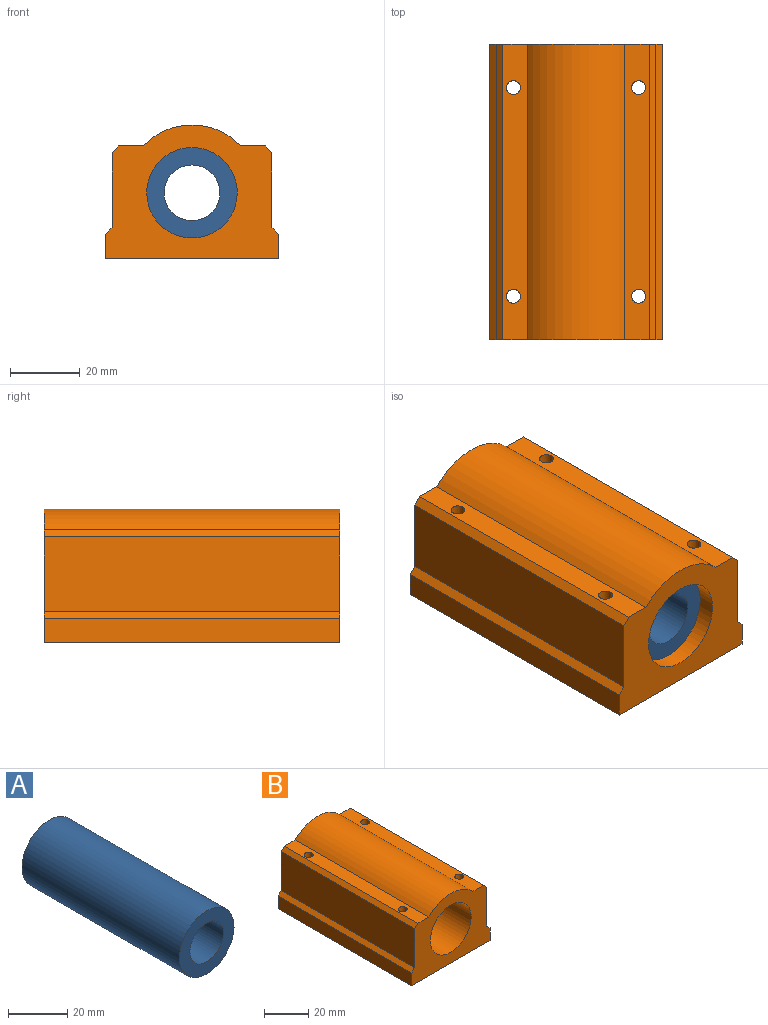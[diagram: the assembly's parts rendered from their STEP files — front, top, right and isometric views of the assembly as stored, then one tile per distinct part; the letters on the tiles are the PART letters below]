
ASSEMBLY  parts=2 mates=1
PART A: 4 faces, bbox 26x75x26 mm
  f0: plane 26x26mm, normal (0,-1,0), area 329.9mm2, adj f1,f2
  f1: cylinder r=8mm len=75mm, axis (0,1,0), area 3769.9mm2, adj f0,f3
  f2: cylinder r=13mm len=75mm, axis (0,1,0), area 6126.1mm2, adj f0,f3
  f3: plane 26x26mm, normal (0,1,0), area 329.9mm2, adj f1,f2
PART B: 27 faces, bbox 50x85x38.5 mm
  f0: cylinder r=2mm len=20.5mm, axis (0,0,-1), area 257.6mm2, adj f12,f25
  f1: cylinder r=2mm len=20.5mm, axis (0,0,-1), area 257.6mm2, adj f12,f23
  f2: cylinder r=2mm len=20.5mm, axis (0,0,-1), area 257.6mm2, adj f4,f21
  f3: cylinder r=2mm len=20.5mm, axis (0,0,-1), area 257.6mm2, adj f4,f19
  f4: plane 85x6.93mm, normal (0,0,1), area 563.8mm2, adj f2,f3,f6,f8,f13,f14
  f5: plane 85x7mm, normal (-1,0,0), area 595mm2, adj f6,f8,f9,f17
  f6: plane 50x38.5mm, normal (0,-1,0), area 1108.6mm2, adj f4,f5,f7,f9,f10,f11,f12,f13
  f7: plane 85x7mm, normal (1,0,0), area 595mm2, adj f6,f8,f9,f16
  f8: plane 50x38.5mm, normal (0,1,0), area 1108.6mm2, adj f4,f5,f7,f9,f10,f11,f12,f13
  f9: plane 85x50mm, normal (0,0,-1), area 4171.5mm2, adj f5,f6,f7,f8,f20,f22,f24,f26
  f10: plane 85x21.5mm, normal (-1,0,0), area 1827.5mm2, adj f6,f8,f14,f17
  f11: plane 85x21.5mm, normal (1,0,0), area 1827.5mm2, adj f6,f8,f15,f16
  f12: plane 85x6.93mm, normal (0,0,1), area 563.8mm2, adj f0,f1,f6,f8,f13,f15
  f13: cylinder r=19.5mm len=85mm, axis (0,1,0), area 2672.3mm2, adj f4,f6,f8,f12
  f14: plane 85x2mm, normal (-0.71,0,0.71), area 240.4mm2, adj f4,f6,f8,f10
  f15: plane 85x2mm, normal (0.71,0,0.71), area 240.4mm2, adj f6,f8,f11,f12
  f16: plane 85x2mm, normal (0.71,0,0.71), area 240.4mm2, adj f6,f7,f8,f11
  f17: plane 85x2mm, normal (-0.71,0,0.71), area 240.4mm2, adj f5,f6,f8,f10
  f18: cylinder r=13mm len=85mm, axis (0,1,0), area 6942.9mm2, adj f6,f8
  f19: plane 5x5mm, normal (0,0,-1), area 7.1mm2, adj f3,f20
  f20: cylinder r=2.5mm len=12mm, axis (0,0,-1), area 188.5mm2, adj f9,f19
  f21: plane 5x5mm, normal (0,0,-1), area 7.1mm2, adj f2,f22
  f22: cylinder r=2.5mm len=12mm, axis (0,0,-1), area 188.5mm2, adj f9,f21
  f23: plane 5x5mm, normal (0,0,-1), area 7.1mm2, adj f1,f24
  f24: cylinder r=2.5mm len=12mm, axis (0,0,-1), area 188.5mm2, adj f9,f23
  f25: plane 5x5mm, normal (0,0,-1), area 7.1mm2, adj f0,f26
  f26: cylinder r=2.5mm len=12mm, axis (0,0,-1), area 188.5mm2, adj f9,f25
PLACE A t=(-1.96,11.83,0.19)mm
PLACE B t=(-1.96,11.83,0.19)mm
MATE fastened A.f1 <-> B.f18  axis (0,-1,0) through (-1.96,-30.67,19.19)mm
